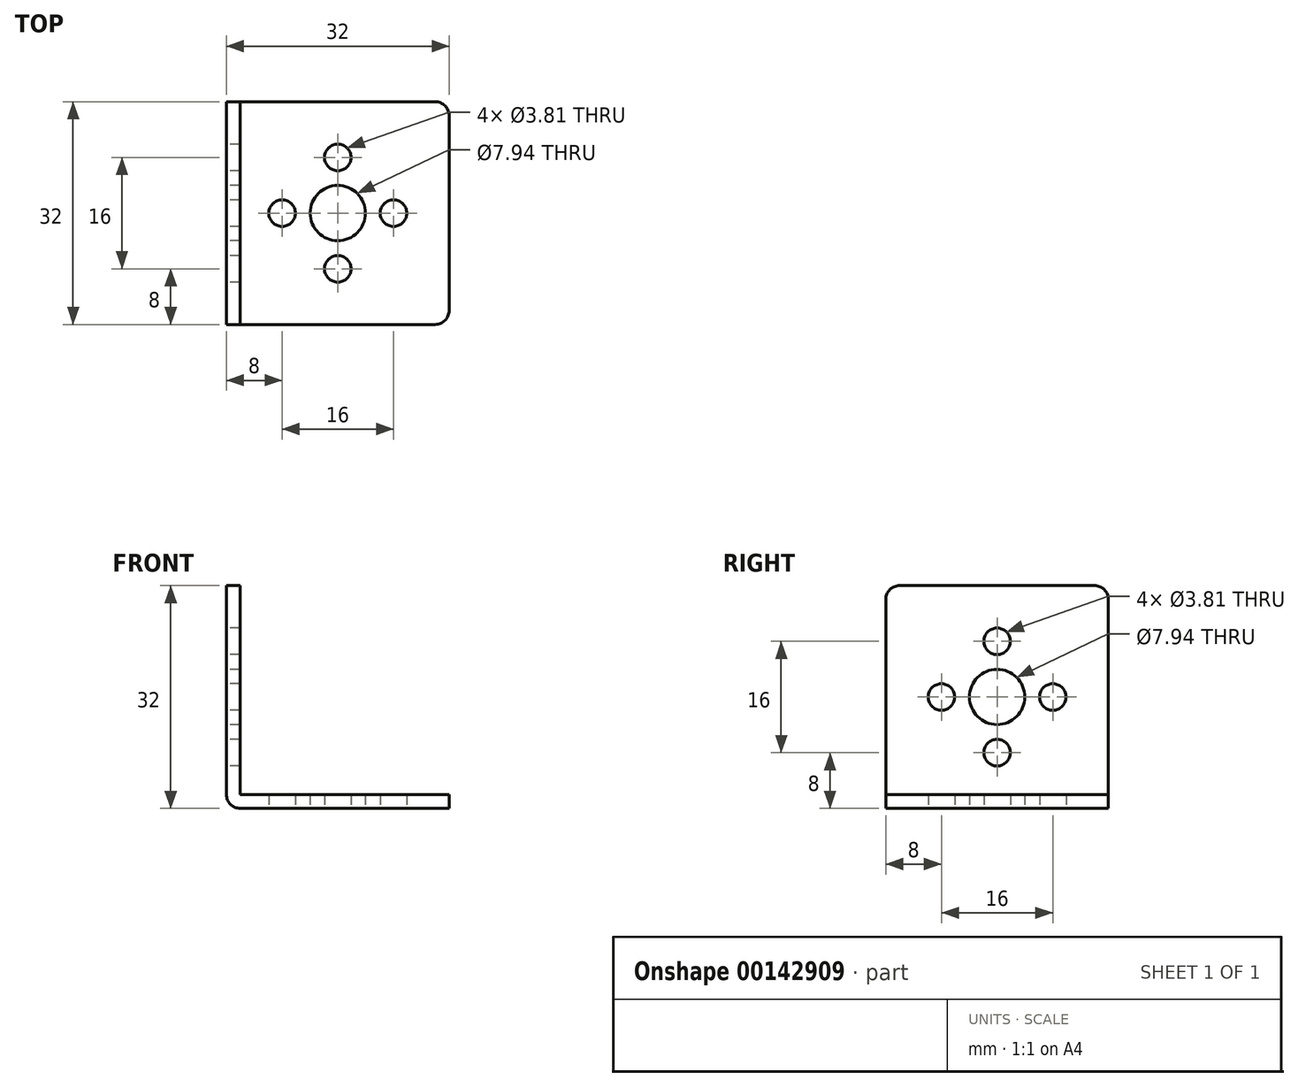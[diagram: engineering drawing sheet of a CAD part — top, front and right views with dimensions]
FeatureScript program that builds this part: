
annotation { "Feature Type Name" : "Feature", "Feature Type Description" : "" }
export const myFeature = defineFeature(function(context is Context, id is Id, definition is map)
    precondition{}
    {
        {
            var Q0;
            Q0=qCreatedBy(makeId("Top.planeOp"),FACE);
            var sketch = newSketch(context, id + "F0", { "sketchPlane" : qUnion([Q0])});
            skLineSegment(sketch, "E0.bottom", {"start": v(0, 0) * mm, "end": v(-32, 0) * mm});
            skLineSegment(sketch, "E0.top", {"start": v(0, 32) * mm, "end": v(-32, 32) * mm});
            skLineSegment(sketch, "E0.left", {"start": v(0, 0) * mm, "end": v(0, 32) * mm});
            skLineSegment(sketch, "E0.right", {"start": v(-32, 0) * mm, "end": v(-32, 32) * mm});
            skCircle(sketch, "E1", {"center": v(-16, 16) * mm, "radius": 3.97 * mm});
            skPoint(sketch, "E1.centerSnap0", {"position": v(0, 16) * mm});
            skPoint(sketch, "E1.centerSnap1", {"position": v(-16, 32) * mm});
            skCircle(sketch, "E2", {"center": v(-16, 24) * mm, "radius": 1.9 * mm});
            skCircle(sketch, "E3.1.0", {"center": v(-24, 16) * mm, "radius": 1.9 * mm});
            skCircle(sketch, "E3.2.0", {"center": v(-16, 8) * mm, "radius": 1.9 * mm});
            skCircle(sketch, "E3.3.0", {"center": v(-8, 16) * mm, "radius": 1.9 * mm});
            skSolve(sketch);
        }
        {
            var Q0;
            Q0=makeQuery(id+"F0.imprint","IMPRINT",FACE,{"disambiguationData":[TD([[makeQuery(id+"F0.imprint","IMPRINT",EDGE,{"derivedFrom":sQuery(id+"F0.wireOp",EDGE,"1bb81507-4f5c-4394-839c-011548c47b70.bottom")}),1.0]])]});
            var Q1;
            Q1=makeQuery(id+"F0.imprint","IMPRINT",FACE,{"disambiguationData":[TD([[makeQuery(id+"F0.imprint","IMPRINT",EDGE,{"derivedFrom":sQuery(id+"F0.wireOp",EDGE,"E0.bottom")}),-1.0]])]});
            extrude(context, id + "F1", {"entities" : qUnion([Q0, Q1]), "depth" : 2 * mm});
        }
        {
            var Q0;
            Q0=makeQuery(id+"F1.opExtrude","CAP_FACE",FACE,{"disambiguationData":[OSD([sQuery(id+"F0.wireOp",EDGE,"E0.bottom"),sQuery(id+"F0.wireOp",EDGE,"E0.top"),sQuery(id+"F0.wireOp",EDGE,"E0.left"),sQuery(id+"F0.wireOp",EDGE,"E0.right"),sQuery(id+"F0.wireOp",EDGE,"E1"),sQuery(id+"F0.wireOp",EDGE,"E2"),sQuery(id+"F0.wireOp",EDGE,"E3.1.0"),sQuery(id+"F0.wireOp",EDGE,"E3.2.0"),sQuery(id+"F0.wireOp",EDGE,"E3.3.0")])],"isStart":false});
            var sketch = newSketch(context, id + "F2", { "sketchPlane" : qUnion([Q0])});
            skLineSegment(sketch, "E4.bottom", {"start": v(-32, 0) * mm, "end": v(-30, 0) * mm});
            skLineSegment(sketch, "E4.top", {"start": v(-32, 32) * mm, "end": v(-30, 32) * mm});
            skLineSegment(sketch, "E4.left", {"start": v(-32, 0) * mm, "end": v(-32, 32) * mm});
            skLineSegment(sketch, "E4.right", {"start": v(-30, 0) * mm, "end": v(-30, 32) * mm});
            skSolve(sketch);
        }
        {
            var Q0;
            Q0=makeQuery(id+"F2.imprint","IMPRINT",FACE,{"disambiguationData":[TD([[makeQuery(id+"F2.imprint","IMPRINT",EDGE,{"derivedFrom":sQuery(id+"F2.wireOp",EDGE,"E4.bottom")}),-1.0]])]});
            extrude(context, id + "F3", {"entities" : qUnion([Q0]), "operationType" : NewBodyOperationType.ADD, "depth" : 30 * mm});
        }
        {
            var Q0;
            Q0=makeQuery(id+"F3.boolean.opBoolean","MERGE",FACE,{"derivedFrom":[makeQuery(id+"F1.opExtrude","SWEPT_FACE",FACE,{"disambiguationData":[OSD([sQuery(id+"F0.wireOp",EDGE,"E0.right")])]}),makeQuery(id+"F3.opExtrude","SWEPT_FACE",FACE,{"disambiguationData":[OSD([sQuery(id+"F2.wireOp",EDGE,"E4.left")])]})]});
            var sketch = newSketch(context, id + "F4", { "sketchPlane" : qUnion([Q0])});
            skCircle(sketch, "E5", {"center": v(-16, 16) * mm, "radius": 3.97 * mm});
            skPoint(sketch, "E5.centerSnap0", {"position": v(0, 16) * mm});
            skPoint(sketch, "E5.centerSnap1", {"position": v(-16, 32) * mm});
            skCircle(sketch, "E6", {"center": v(-16, 24) * mm, "radius": 1.9 * mm});
            skCircle(sketch, "E7.1.0", {"center": v(-24, 16) * mm, "radius": 1.9 * mm});
            skCircle(sketch, "E7.2.0", {"center": v(-16, 8) * mm, "radius": 1.9 * mm});
            skCircle(sketch, "E7.3.0", {"center": v(-8, 16) * mm, "radius": 1.9 * mm});
            skSolve(sketch);
        }
        {
            var Q0;
            Q0=qSketchRegion(id+"F4",true);
            extrude(context, id + "F5", {"entities" : qUnion([Q0]), "operationType" : NewBodyOperationType.REMOVE, "endBound" : BoundingType.UP_TO_NEXT, "oppositeDirection" : true, "depth" : 25.4 * mm});
        }
        {
            var Q0;
            Q0=makeQuery(id+"F3.opExtrude","CAP_EDGE",EDGE,{"disambiguationData":[OSD([sQuery(id+"F2.wireOp",EDGE,"E4.bottom")])],"isStart":false});
            var Q1;
            Q1=makeQuery(id+"F3.opExtrude","CAP_EDGE",EDGE,{"disambiguationData":[OSD([sQuery(id+"F2.wireOp",EDGE,"E4.top")])],"isStart":false});
            var Q2;
            Q2=makeQuery(id+"F1.opExtrude","SWEPT_EDGE",EDGE,{"disambiguationData":[OSD([sQuery(id+"F0.wireOp",EDGE,"E0.bottom"),sQuery(id+"F0.wireOp",EDGE,"E0.left")])]});
            var Q3;
            Q3=makeQuery(id+"F1.opExtrude","SWEPT_EDGE",EDGE,{"disambiguationData":[OSD([sQuery(id+"F0.wireOp",EDGE,"E0.top"),sQuery(id+"F0.wireOp",EDGE,"E0.left")])]});
            var Q4;
            Q4=makeQuery(id+"F3.opExtrude","CAP_EDGE",EDGE,{"disambiguationData":[OSD([sQuery(id+"F2.wireOp",EDGE,"E4.right")])],"isStart":true});
            var Q5;
            Q5=makeQuery(id+"F1.opExtrude","CAP_EDGE",EDGE,{"disambiguationData":[OSD([sQuery(id+"F0.wireOp",EDGE,"E0.right")])],"isStart":true});
            fillet(context, id + "F6", {"entities" : qUnion([Q0, Q1, Q2, Q3, Q4, Q5]), "radius" : 2 * mm, "tangentPropagation" : true, "allowEdgeOverflow" : false});
        }
    });
